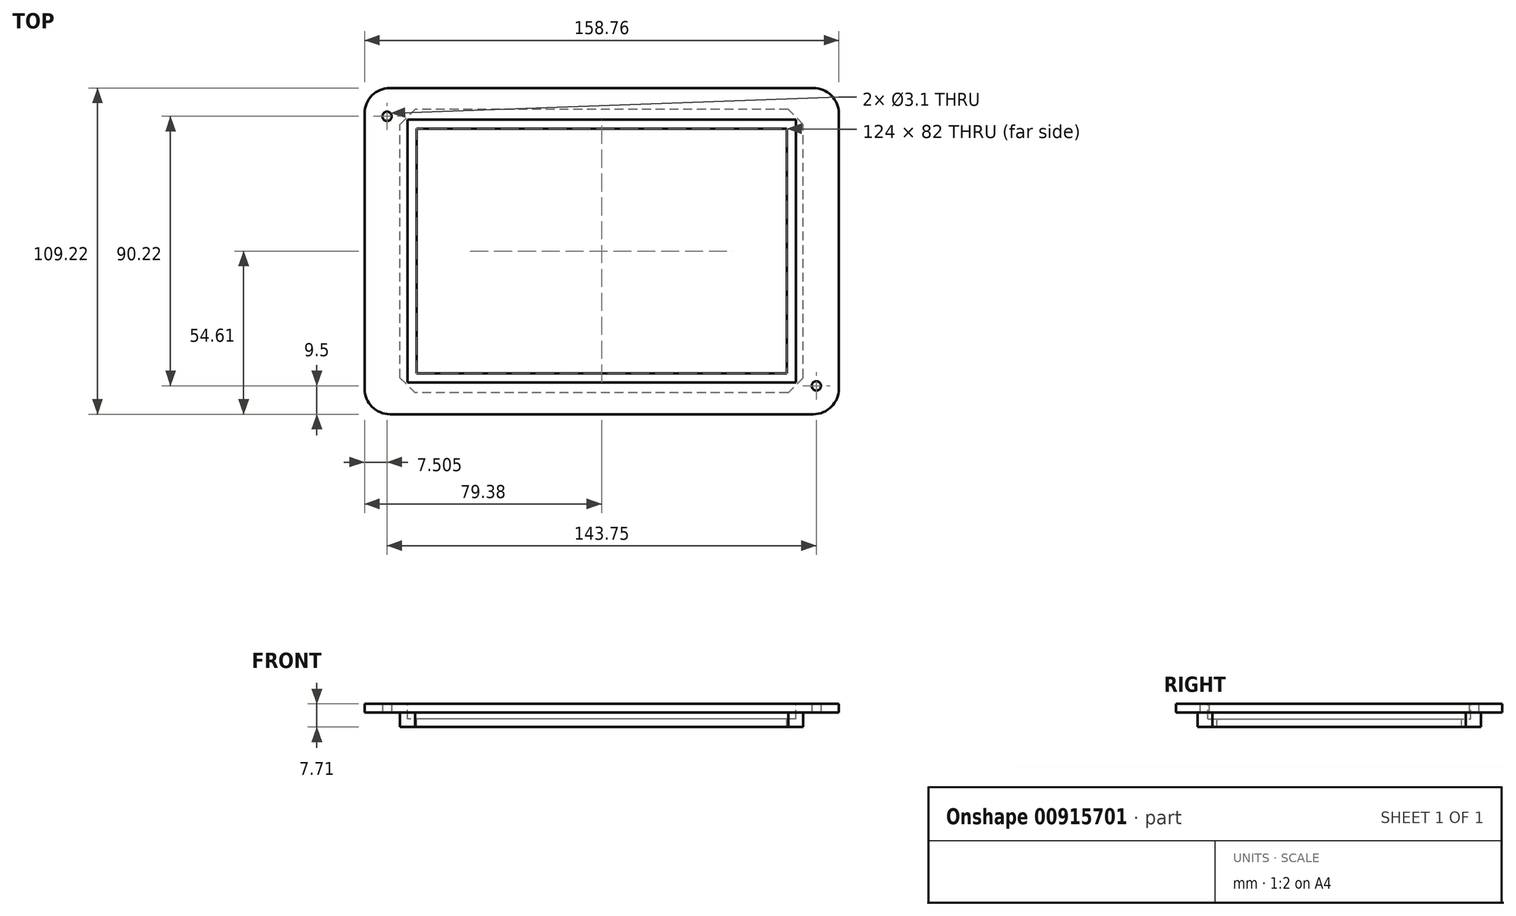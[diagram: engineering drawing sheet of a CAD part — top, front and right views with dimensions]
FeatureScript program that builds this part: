
annotation { "Feature Type Name" : "Feature", "Feature Type Description" : "" }
export const myFeature = defineFeature(function(context is Context, id is Id, definition is map)
    precondition{}
    {
        {
            var Q0;
            Q0=qCreatedBy(makeId("Top.planeOp"),FACE);
            var sketch = newSketch(context, id + "F0", { "sketchPlane" : qUnion([Q0])});
            skLineSegment(sketch, "E0.bottom", {"start": v(79.38, -54.61) * mm, "end": v(-79.38, -54.61) * mm});
            skLineSegment(sketch, "E0.top", {"start": v(79.37, 54.61) * mm, "end": v(-79.38, 54.6) * mm});
            skLineSegment(sketch, "E0.left", {"start": v(79.38, -54.61) * mm, "end": v(79.37, 54.61) * mm});
            skLineSegment(sketch, "E0.right", {"start": v(-79.37, -54.61) * mm, "end": v(-79.38, 54.6) * mm});
            skPoint(sketch, "E0.middle", {"position": v(0, 0) * mm});
            skCircle(sketch, "E1", {"center": v(71.88, -45.11) * mm, "radius": 1.55 * mm});
            skCircle(sketch, "E2", {"center": v(-71.88, 45.11) * mm, "radius": 1.55 * mm});
            skArc(sketch, "E3", {"start": v(79.37, 46.11) * mm, "mid": v(76.89, 52.12) * mm, "end": v(70.87, 54.61) * mm});
            skArc(sketch, "E4.MirrorCS", {"start": v(79.37, -46.11) * mm, "mid": v(76.89, -52.12) * mm, "end": v(70.87, -54.61) * mm});
            skArc(sketch, "E5.MirrorCS", {"start": v(-79.37, 46.11) * mm, "mid": v(-76.89, 52.12) * mm, "end": v(-70.87, 54.61) * mm});
            skArc(sketch, "E6.MirrorCS", {"start": v(-79.37, -46.11) * mm, "mid": v(-76.89, -52.12) * mm, "end": v(-70.87, -54.61) * mm});
            skSolve(sketch);
        }
        {
            var Q0;
            Q0=makeQuery(id+"F0.imprint","IMPRINT",FACE,{"disambiguationData":[TD([[makeQuery(id+"F0.imprint","IMPRINT",EDGE,{"derivedFrom":sQuery(id+"F0.wireOp",EDGE,"E1")}),-1.0]])]});
            extrude(context, id + "F1", {"entities" : qUnion([Q0]), "depth" : 2.91 * mm, "offsetDistance" : 25 * mm});
        }
        {
            var Q0;
            Q0=qCreatedBy(makeId("Top.planeOp"),FACE);
            var sketch = newSketch(context, id + "F2", { "sketchPlane" : qUnion([Q0])});
            skLineSegment(sketch, "E7.bottom", {"start": v(67.5, -47.42) * mm, "end": v(-67.5, -47.43) * mm});
            skLineSegment(sketch, "E7.top", {"start": v(67.5, 47.43) * mm, "end": v(-67.5, 47.42) * mm});
            skLineSegment(sketch, "E7.left", {"start": v(67.5, -47.42) * mm, "end": v(67.5, 47.43) * mm});
            skLineSegment(sketch, "E7.right", {"start": v(-67.5, -47.43) * mm, "end": v(-67.5, 47.42) * mm});
            skPoint(sketch, "E7.middle", {"position": v(0, 0) * mm});
            skLineSegment(sketch, "E8", {"start": v(-67.5, -42.43) * mm, "end": v(-62.5, -47.43) * mm});
            skLineSegment(sketch, "E9.MirrorCS", {"start": v(67.5, -42.43) * mm, "end": v(62.5, -47.43) * mm});
            skLineSegment(sketch, "E10.MirrorCS", {"start": v(-67.5, 42.43) * mm, "end": v(-62.5, 47.43) * mm});
            skLineSegment(sketch, "E11.MirrorCS", {"start": v(67.5, 42.43) * mm, "end": v(62.5, 47.43) * mm});
            skSolve(sketch);
        }
        {
            var Q0;
            {var subQ0=sQuery(id+"F2.wireOp",EDGE,"E8");Q0=makeQuery(id+"F2.imprint","IMPRINT",FACE,{"disambiguationData":[TD([[makeQuery(id+"F2.imprint","IMPRINT",EDGE,{"derivedFrom":subQ0}),1.0]])]});}
            extrude(context, id + "F3", {"entities" : qUnion([Q0]), "operationType" : NewBodyOperationType.ADD, "depth" : -4.8 * mm, "offsetDistance" : 25 * mm});
        }
        {
            var Q0;
            Q0=makeQuery(id+"F1.opExtrude","CAP_FACE",FACE,{"disambiguationData":[OSD([sQuery(id+"F0.wireOp",EDGE,"E0.bottom"),sQuery(id+"F0.wireOp",EDGE,"E0.top"),sQuery(id+"F0.wireOp",EDGE,"E0.left"),sQuery(id+"F0.wireOp",EDGE,"E0.right"),sQuery(id+"F0.wireOp",EDGE,"E1"),sQuery(id+"F0.wireOp",EDGE,"E2"),sQuery(id+"F0.wireOp",EDGE,"E3"),sQuery(id+"F0.wireOp",EDGE,"E4.MirrorCS"),sQuery(id+"F0.wireOp",EDGE,"E5.MirrorCS"),sQuery(id+"F0.wireOp",EDGE,"E6.MirrorCS")])],"isStart":false});
            var sketch = newSketch(context, id + "F4", { "sketchPlane" : qUnion([Q0])});
            skLineSegment(sketch, "E12.bottom", {"start": v(65, -44) * mm, "end": v(-65, -44) * mm});
            skLineSegment(sketch, "E12.top", {"start": v(65, 44) * mm, "end": v(-65, 44) * mm});
            skLineSegment(sketch, "E12.left", {"start": v(65, -44) * mm, "end": v(65, 44) * mm});
            skLineSegment(sketch, "E12.right", {"start": v(-65, -44) * mm, "end": v(-65, 44) * mm});
            skPoint(sketch, "E12.middle", {"position": v(0, 0) * mm});
            skLineSegment(sketch, "E13.bottom", {"start": v(62, -41) * mm, "end": v(-62, -41) * mm});
            skLineSegment(sketch, "E13.top", {"start": v(62, 41) * mm, "end": v(-62, 41) * mm});
            skLineSegment(sketch, "E13.left", {"start": v(62, -41) * mm, "end": v(62, 41) * mm});
            skLineSegment(sketch, "E13.right", {"start": v(-62, -41) * mm, "end": v(-62, 41) * mm});
            skSolve(sketch);
        }
        {
            var Q0;
            Q0=makeQuery(id+"F4.imprint","IMPRINT",FACE,{"disambiguationData":[TD([[makeQuery(id+"F4.imprint","IMPRINT",EDGE,{"derivedFrom":sQuery(id+"F4.wireOp",EDGE,"E12.bottom")}),-1.0]])]});
            var Q1;
            Q1=makeQuery(id+"F4.imprint","IMPRINT",FACE,{"disambiguationData":[TD([[makeQuery(id+"F4.imprint","IMPRINT",EDGE,{"derivedFrom":sQuery(id+"F4.wireOp",EDGE,"E13.bottom")}),-1.0]])]});
            extrude(context, id + "F5", {"entities" : qUnion([Q0, Q1]), "operationType" : NewBodyOperationType.REMOVE, "oppositeDirection" : true, "depth" : (5) * mm, "offsetDistance" : 25 * mm});
        }
        {
            var Q0;
            Q0=makeQuery(id+"F4.imprint","IMPRINT",FACE,{"disambiguationData":[TD([[makeQuery(id+"F4.imprint","IMPRINT",EDGE,{"derivedFrom":sQuery(id+"F4.wireOp",EDGE,"E13.bottom")}),-1.0]])]});
            extrude(context, id + "F6", {"entities" : qUnion([Q0]), "operationType" : NewBodyOperationType.REMOVE, "oppositeDirection" : true, "depth" : 25 * mm, "offsetDistance" : 25 * mm});
        }
    });
